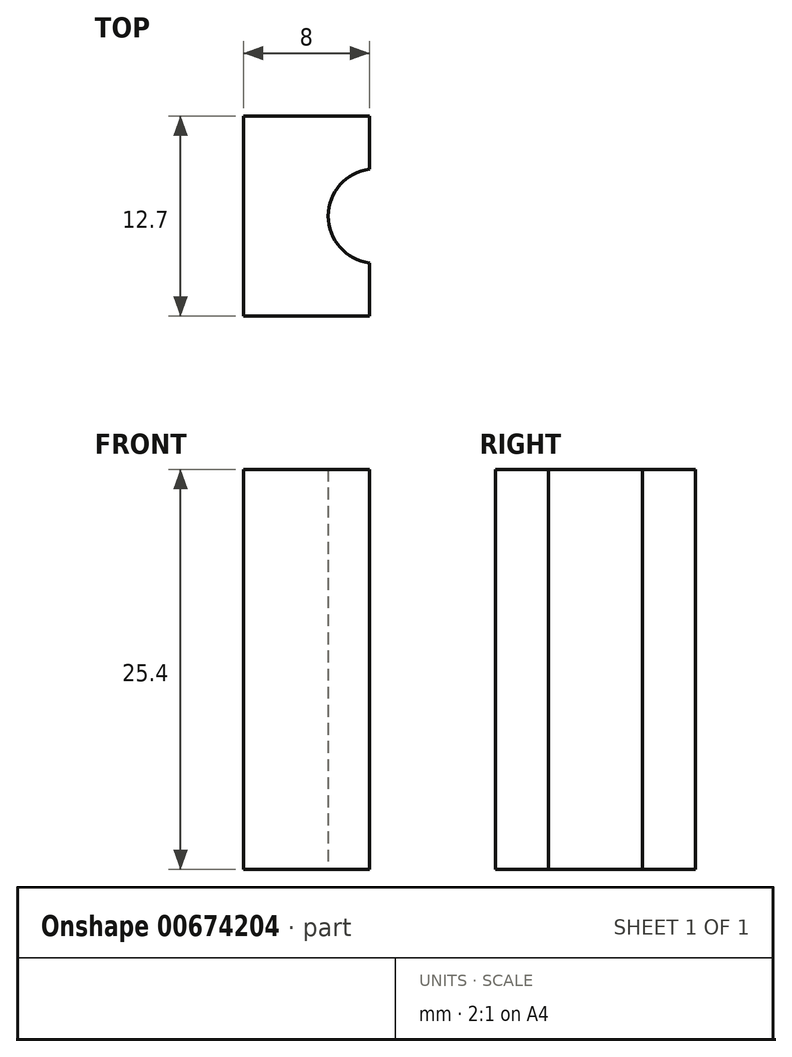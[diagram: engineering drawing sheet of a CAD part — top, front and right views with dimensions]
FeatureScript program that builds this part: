
annotation { "Feature Type Name" : "Feature", "Feature Type Description" : "" }
export const myFeature = defineFeature(function(context is Context, id is Id, definition is map)
    precondition{}
    {
        {
            var Q0;
            Q0=qCreatedBy(makeId("Top.planeOp"),FACE);
            var sketch = newSketch(context, id + "F0", { "sketchPlane" : qUnion([Q0])});
            skLineSegment(sketch, "E0.bottom", {"start": v(-8, 6.35) * mm, "end": v(0, 6.35) * mm});
            skLineSegment(sketch, "E0.top", {"start": v(-8, 0) * mm, "end": v(0, 0) * mm});
            skLineSegment(sketch, "E0.left", {"start": v(-8, 6.35) * mm, "end": v(-8, 0) * mm});
            skLineSegment(sketch, "E0.right", {"start": v(0, 6.35) * mm, "end": v(0, 0) * mm});
            skLineSegment(sketch, "E1.top", {"start": v(-8, -6.35) * mm, "end": v(0, -6.35) * mm});
            skLineSegment(sketch, "E1.left", {"start": v(-8, 0) * mm, "end": v(-8, -6.35) * mm});
            skLineSegment(sketch, "E1.right", {"start": v(0, 0) * mm, "end": v(0, -6.35) * mm});
            skArc(sketch, "E2", {"start": v(0, 2.98) * mm, "mid": v(-2.62, 0) * mm, "end": v(0, -2.98) * mm});
            skSolve(sketch);
        }
        {
            var Q0;
            {var subQ1=sQuery(id+"F0.wireOp",EDGE,"E1.top");Q0=makeQuery(id+"F0.imprint","IMPRINT",FACE,{"disambiguationData":[TD([[makeQuery(id+"F0.imprint","IMPRINT",EDGE,{"derivedFrom":subQ1}),1.0]])]});}
            var Q1;
            {var subQ5=sQuery(id+"F0.wireOp",EDGE,"E0.bottom");Q1=makeQuery(id+"F0.imprint","IMPRINT",FACE,{"disambiguationData":[TD([[makeQuery(id+"F0.imprint","IMPRINT",EDGE,{"derivedFrom":subQ5}),-1.0]])]});}
            extrude(context, id + "F1", {"entities" : qUnion([Q0, Q1]), "depth" : 25.4 * mm, "offsetDistance" : 25 * mm});
        }
    });
